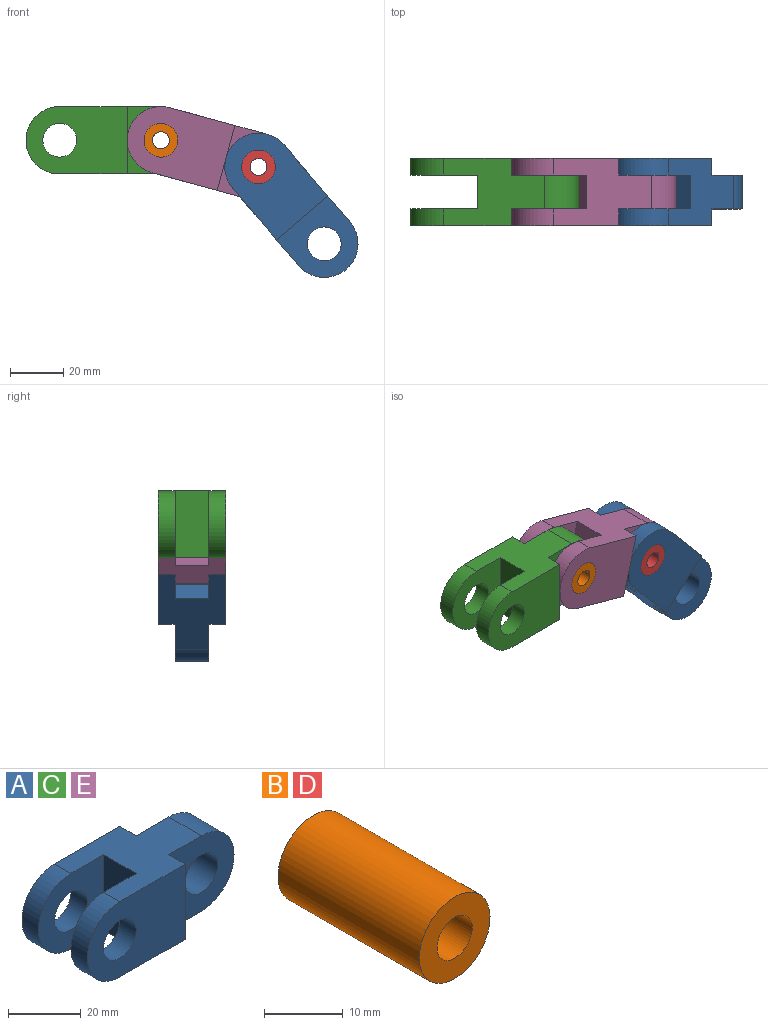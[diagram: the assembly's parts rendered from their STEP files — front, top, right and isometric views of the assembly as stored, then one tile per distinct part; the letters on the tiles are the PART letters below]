
ASSEMBLY  parts=5 mates=4
PART A: 17 faces, bbox 63.5x25.4x25.4 mm
  f0: cylinder r=12.7mm len=25.4mm, axis (0,1,0), area 253.4mm2, adj f1,f3,f5,f7
  f1: plane 38.1x25.4mm, normal (0,0,-1), area 645.2mm2, adj f0,f2,f4,f5,f6,f7,f8,f9
  f2: cylinder r=12.7mm len=25.4mm, axis (0,1,0), area 506.7mm2, adj f1,f3,f10,f12
  f3: plane 38.1x25.4mm, normal (0,0,1), area 645.2mm2, adj f0,f2,f4,f5,f6,f7,f8,f9
  f4: plane 38.1x25.4mm, normal (0,-1,0), area 771.8mm2, adj f1,f3,f6,f11,f14
  f5: plane 38.1x25.4mm, normal (0,1,0), area 771.8mm2, adj f0,f1,f3,f13,f15
  f6: cylinder r=12.7mm len=25.4mm, axis (0,1,0), area 253.4mm2, adj f1,f3,f4,f8
  f7: plane 25.4x25.4mm, normal (0,-1,0), area 449.3mm2, adj f0,f1,f3,f9,f15
  f8: plane 25.4x25.4mm, normal (0,1,0), area 449.3mm2, adj f1,f3,f6,f9,f14
  f9: plane 25.4x12.7mm, normal (-1,0,0), area 322.6mm2, adj f1,f3,f7,f8
  f10: plane 25.4x25.4mm, normal (0,-1,0), area 449.3mm2, adj f1,f2,f3,f11,f16
  f11: plane 25.4x6.35mm, normal (1,0,0), area 161.3mm2, adj f1,f3,f4,f10
  f12: plane 25.4x25.4mm, normal (0,1,0), area 449.3mm2, adj f1,f2,f3,f13,f16
  f13: plane 25.4x6.35mm, normal (1,0,0), area 161.3mm2, adj f1,f3,f5,f12
  f14: cylinder r=6.35mm len=12.7mm, axis (0,-1,0), area 253.4mm2, adj f4,f8
  f15: cylinder r=6.35mm len=12.7mm, axis (0,-1,0), area 253.4mm2, adj f5,f7
  f16: cylinder r=6.35mm len=12.7mm, axis (0,-1,0), area 506.7mm2, adj f10,f12
PART B: 4 faces, bbox 12.7x25.4x12.7 mm
  f0: cylinder r=3.17mm len=25.4mm, axis (0,1,0), area 506.7mm2, adj f2,f3
  f1: cylinder r=6.35mm len=25.4mm, axis (0,1,0), area 1013.4mm2, adj f2,f3
  f2: plane 12.7x12.7mm, normal (0,-1,0), area 95mm2, adj f0,f1
  f3: plane 12.7x12.7mm, normal (0,1,0), area 95mm2, adj f0,f1
PART C: same geometry as A
PART D: same geometry as B
PART E: same geometry as A
PLACE A rot(axis=(0,1,0),49.5deg) t=(-8.57,-0.03,26.65)mm
PLACE B rot(axis=(0,1,0),15.2deg) t=(-45.33,-0.03,36.66)mm
PLACE C t=(-83.43,-0.03,36.66)mm fixed
PLACE D rot(axis=(0,1,0),49.5deg) t=(-8.57,-0.03,26.65)mm
PLACE E rot(axis=(0,1,0),15.2deg) t=(-45.33,-0.03,36.66)mm
MATE revolute B.f1 <-> C.f16  axis (0,1,0) through (-45.33,-12.73,36.66)mm
MATE revolute D.f1 <-> E.f16  axis (0,1,0) through (-8.57,-12.73,26.65)mm
MATE fastened D.f0 <-> A.f14  axis (0,-1,0) through (-8.57,-25.43,26.65)mm
MATE fastened B.f0 <-> E.f14  axis (0,1,0) through (-45.33,-25.43,36.66)mm
